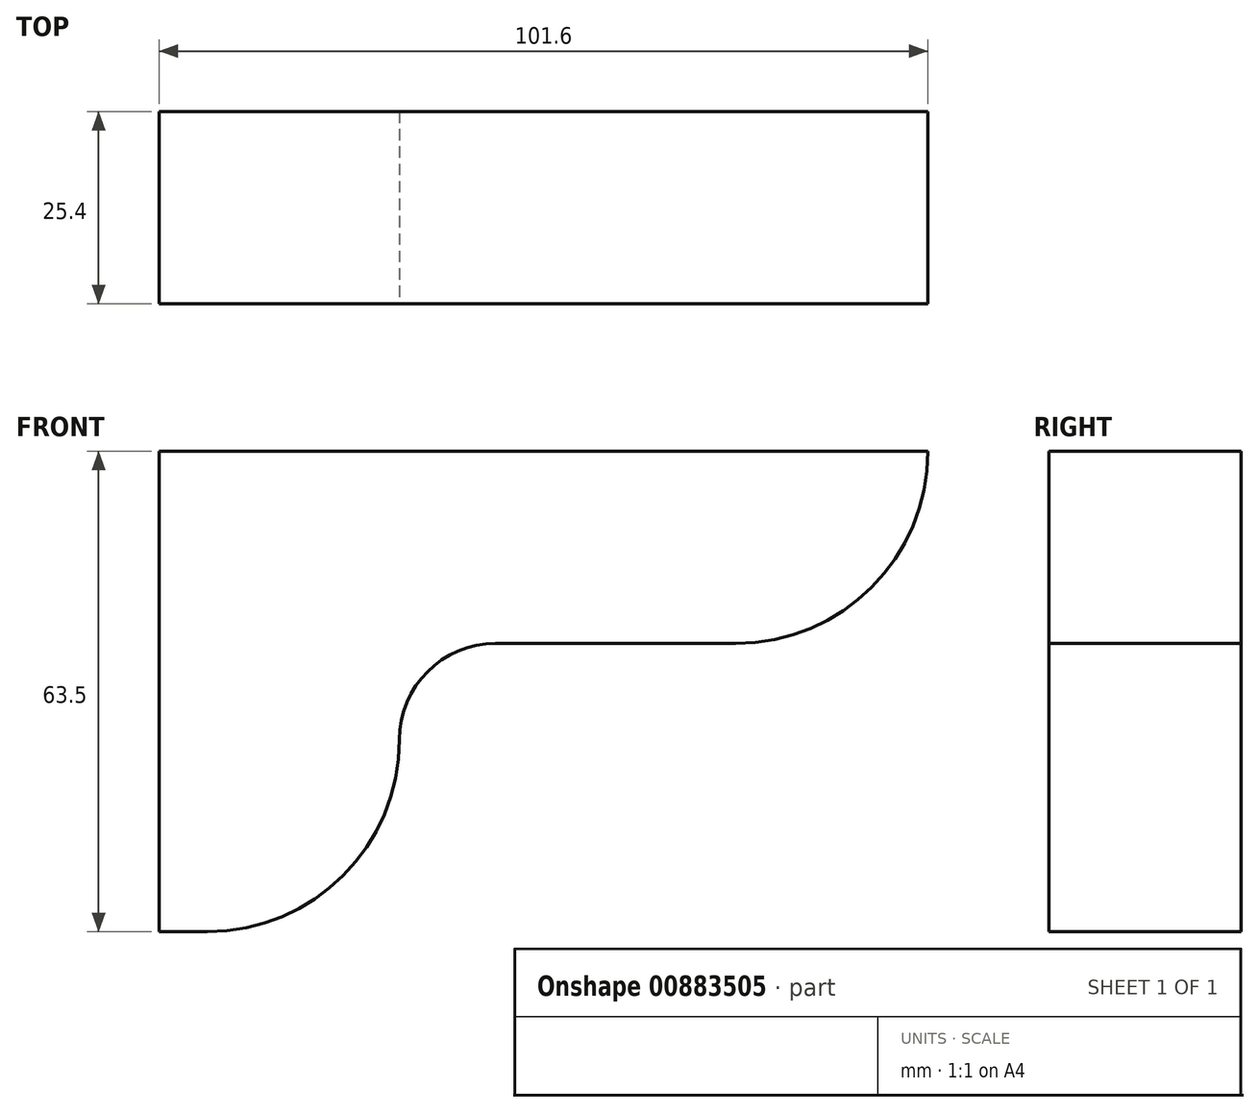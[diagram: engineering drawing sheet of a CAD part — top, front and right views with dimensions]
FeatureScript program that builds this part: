
annotation { "Feature Type Name" : "Feature", "Feature Type Description" : "" }
export const myFeature = defineFeature(function(context is Context, id is Id, definition is map)
    precondition{}
    {
        {
            var Q0;
            Q0=qCreatedBy(makeId("Front.planeOp"),FACE);
            var sketch = newSketch(context, id + "F0", { "sketchPlane" : qUnion([Q0])});
            skLineSegment(sketch, "E0.bottom", {"start": v(0, 0) * mm, "end": v(101.6, 0) * mm});
            skLineSegment(sketch, "E0.top", {"start": v(0, -63.5) * mm, "end": v(6.35, -63.5) * mm});
            skLineSegment(sketch, "E0.left", {"start": v(0, -63.5) * mm, "end": v(0, 0) * mm});
            skLineSegment(sketch, "E0.right", {"start": v(101.6, -63.5) * mm, "end": v(101.6, 0) * mm, "construction": true});
            skLineSegment(sketch, "E1", {"start": v(6.35, -63.5) * mm, "end": v(101.6, -63.5) * mm, "construction": true});
            skArc(sketch, "E2", {"start": v(6.35, -63.5) * mm, "mid": v(24.31, -56.06) * mm, "end": v(31.75, -38.1) * mm});
            skArc(sketch, "E3", {"start": v(44.45, -25.4) * mm, "mid": v(35.47, -29.12) * mm, "end": v(31.75, -38.1) * mm});
            skLineSegment(sketch, "E4", {"start": v(44.45, -25.4) * mm, "end": v(76.2, -25.4) * mm});
            skArc(sketch, "E5", {"start": v(76.2, -25.4) * mm, "mid": v(94.16, -17.96) * mm, "end": v(101.6, 0) * mm});
            skSolve(sketch);
        }
        {
            var Q0;
            Q0=qSketchRegion(id+"F0",true);
            extrude(context, id + "F1", {"entities" : qUnion([Q0]), "oppositeDirection" : true, "depth" : 25.4 * mm, "offsetDistance" : 25.4 * mm});
        }
    });
